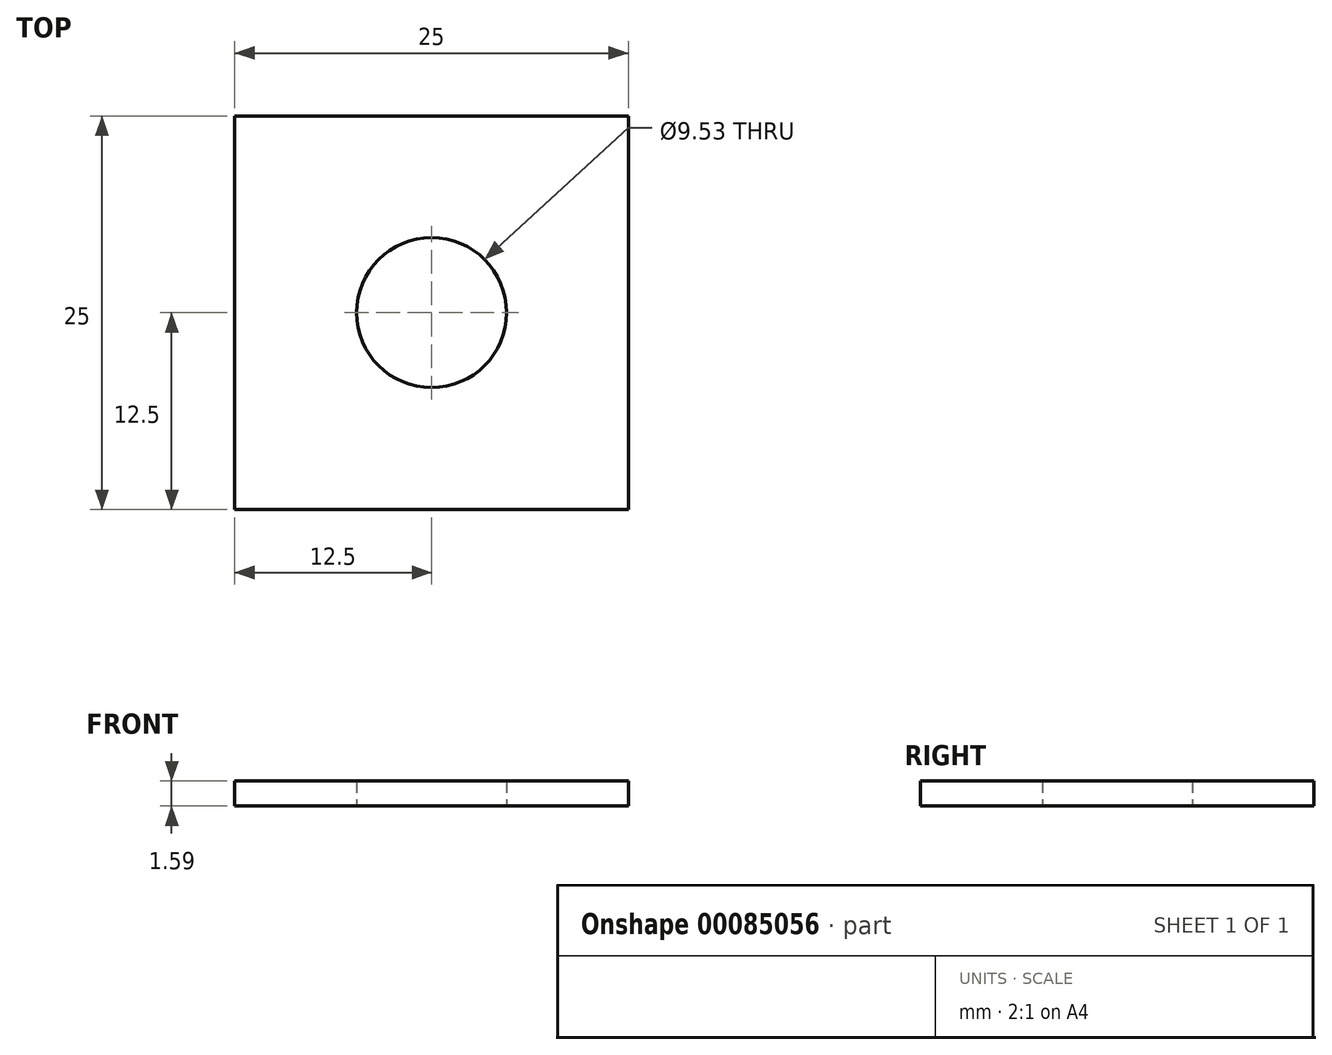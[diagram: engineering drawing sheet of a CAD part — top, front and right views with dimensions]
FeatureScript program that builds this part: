
annotation { "Feature Type Name" : "Feature", "Feature Type Description" : "" }
export const myFeature = defineFeature(function(context is Context, id is Id, definition is map)
    precondition{}
    {
        {
            var Q0;
            Q0=qCreatedBy(makeId("Top.planeOp"),FACE);
            var sketch = newSketch(context, id + "F0", { "sketchPlane" : qUnion([Q0])});
            skLineSegment(sketch, "E0.bottom", {"start": v(12.5, -12.5) * mm, "end": v(-12.5, -12.5) * mm});
            skLineSegment(sketch, "E0.top", {"start": v(12.5, 12.5) * mm, "end": v(-12.5, 12.5) * mm});
            skLineSegment(sketch, "E0.left", {"start": v(12.5, -12.5) * mm, "end": v(12.5, 12.5) * mm});
            skLineSegment(sketch, "E0.right", {"start": v(-12.5, -12.5) * mm, "end": v(-12.5, 12.5) * mm});
            skPoint(sketch, "E0.middle", {"position": v(0, 0) * mm});
            skCircle(sketch, "E1", {"center": v(0, 0) * mm, "radius": 4.76 * mm});
            skSolve(sketch);
        }
        {
            var Q0;
            Q0 = qSketchRegion(id + "F0", true);
            extrude(context, id + "F1", {"entities" : qUnion([Q0]), "depth" : 1.59 * mm});
        }
    });
